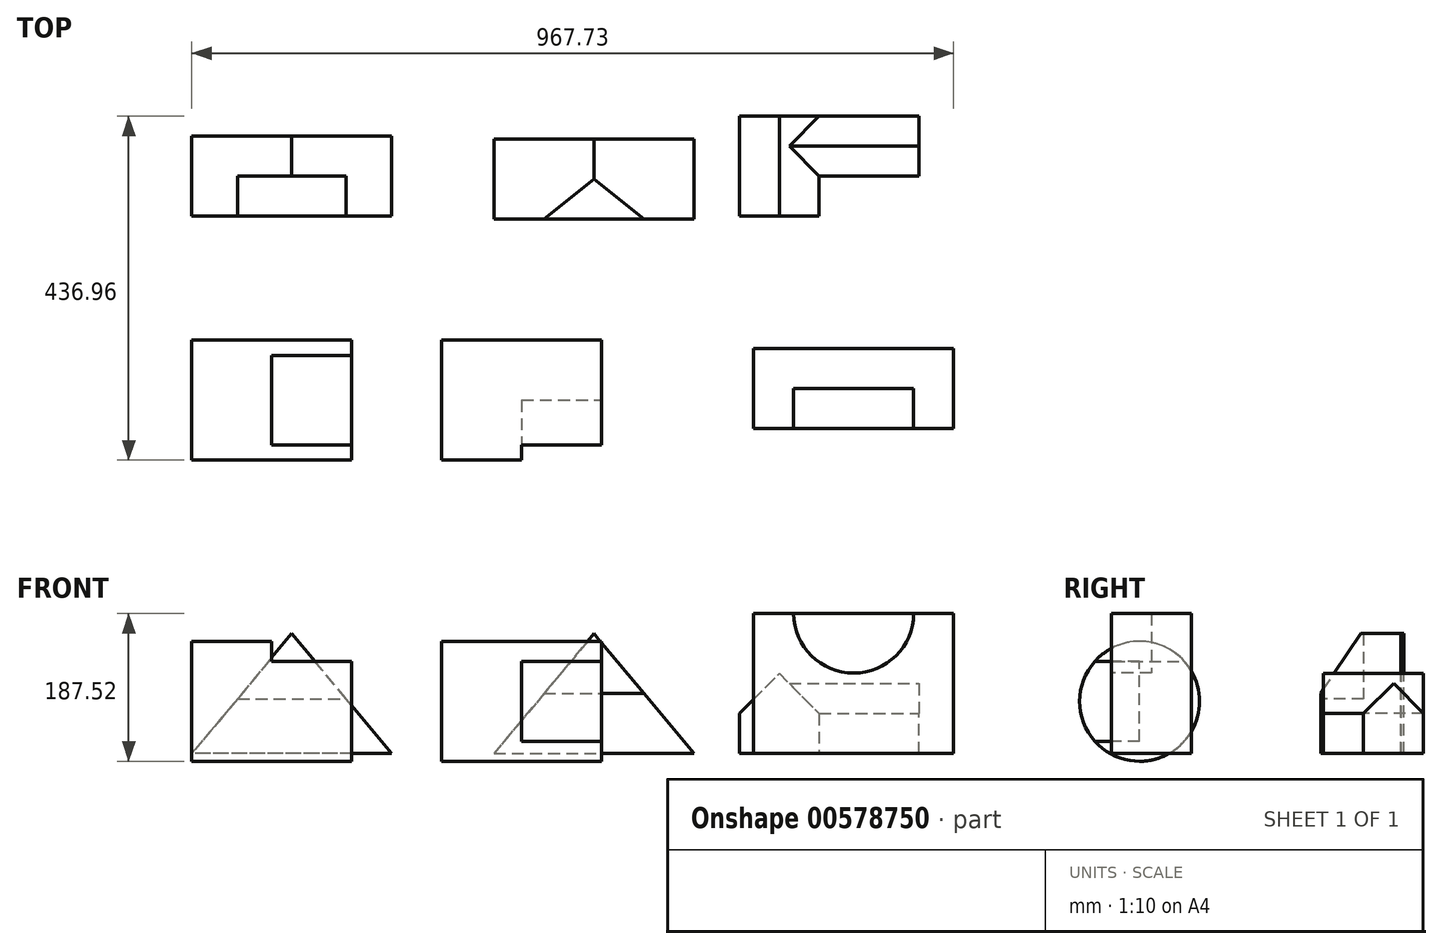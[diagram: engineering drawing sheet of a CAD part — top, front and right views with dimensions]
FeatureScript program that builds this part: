
annotation { "Feature Type Name" : "Feature", "Feature Type Description" : "" }
export const myFeature = defineFeature(function(context is Context, id is Id, definition is map)
    precondition{}
    {
        {
            var Q0;
            Q0=qCreatedBy(makeId("Right.planeOp"),FACE);
            var sketch = newSketch(context, id + "F0", { "sketchPlane" : qUnion([Q0])});
            skLineSegment(sketch, "E0", {"start": v(0, 0) * mm, "end": v(101.6, 0) * mm});
            skLineSegment(sketch, "E1", {"start": v(101.6, 0) * mm, "end": v(101.6, 152.4) * mm});
            skLineSegment(sketch, "E2", {"start": v(101.6, 152.4) * mm, "end": v(0, 152.4) * mm});
            skLineSegment(sketch, "E3", {"start": v(0, 152.4) * mm, "end": v(0, 0) * mm});
            skSolve(sketch);
        }
        {
            var Q0;
            Q0=makeQuery(id+"F0.imprint","IMPRINT",FACE,{"disambiguationData":[TD([[makeQuery(id+"F0.imprint","IMPRINT",EDGE,{"derivedFrom":sQuery(id+"F0.wireOp",EDGE,"E0")}),1.0]])]});
            extrude(context, id + "F1", {"entities" : qUnion([Q0]), "depth" : 254 * mm, "offsetDistance" : 25.4 * mm});
        }
        {
            var Q0;
            Q0=makeQuery(id+"F1.opExtrude","SWEPT_FACE",FACE,{"disambiguationData":[OSD([sQuery(id+"F0.wireOp",EDGE,"E3")])]});
            var sketch = newSketch(context, id + "F2", { "sketchPlane" : qUnion([Q0])});
            skLineSegment(sketch, "E4", {"start": v(127, 152.4) * mm, "end": v(0, 0) * mm});
            skLineSegment(sketch, "E5", {"start": v(0, 0) * mm, "end": v(254, 0) * mm});
            skLineSegment(sketch, "E6", {"start": v(254, 0) * mm, "end": v(127, 152.4) * mm});
            skSolve(sketch);
        }
        {
            var Q0;
            {var subQ0=sQuery(id+"F2.wireOp",EDGE,"E4");Q0=makeQuery(id+"F2.imprint","IMPRINT",FACE,{"disambiguationData":[TD([[makeQuery(id+"F2.imprint","IMPRINT",EDGE,{"derivedFrom":subQ0}),-1.0]])]});}
            extrude(context, id + "F3", {"entities" : qUnion([Q0]), "operationType" : NewBodyOperationType.REMOVE, "oppositeDirection" : true, "depth" : 101.6 * mm, "offsetDistance" : 25.4 * mm});
        }
        {
            var Q0;
            Q0=makeQuery(id+"F1.opExtrude","CAP_FACE",FACE,{"disambiguationData":[OSD([sQuery(id+"F0.wireOp",EDGE,"E0"),sQuery(id+"F0.wireOp",EDGE,"E1"),sQuery(id+"F0.wireOp",EDGE,"E2"),sQuery(id+"F0.wireOp",EDGE,"E3")])],"isStart":false});
            var sketch = newSketch(context, id + "F4", { "sketchPlane" : qUnion([Q0])});
            skLineSegment(sketch, "E7", {"start": v(0, 0) * mm, "end": v(0, 69.72) * mm});
            skLineSegment(sketch, "E8", {"start": v(0, 69.72) * mm, "end": v(50.8, 69.72) * mm});
            skLineSegment(sketch, "E9", {"start": v(50.8, 69.72) * mm, "end": v(50.8, 152.4) * mm});
            skLineSegment(sketch, "E10", {"start": v(50.8, 152.4) * mm, "end": v(101.6, 152.4) * mm});
            skLineSegment(sketch, "E11", {"start": v(101.6, 152.4) * mm, "end": v(101.6, 0) * mm});
            skLineSegment(sketch, "E12", {"start": v(101.6, 0) * mm, "end": v(0, 0) * mm});
            skSolve(sketch);
        }
        {
            var Q0;
            {var subQ0=sQuery(id+"F4.wireOp",EDGE,"E8");Q0=makeQuery(id+"F4.imprint","IMPRINT",FACE,{"disambiguationData":[TD([[makeQuery(id+"F4.imprint","IMPRINT",EDGE,{"derivedFrom":subQ0}),1.0]])]});}
            extrude(context, id + "F5", {"entities" : qUnion([Q0]), "operationType" : NewBodyOperationType.REMOVE, "oppositeDirection" : true, "depth" : 249.43 * mm, "offsetDistance" : 25.4 * mm});
        }
        {
            var Q0;
            Q0=qCreatedBy(makeId("Top.planeOp"),FACE);
            var sketch = newSketch(context, id + "F6", { "sketchPlane" : qUnion([Q0])});
            skLineSegment(sketch, "E13.bottom", {"start": v(383.68, -3.7) * mm, "end": v(637.68, -3.7) * mm});
            skLineSegment(sketch, "E13.top", {"start": v(383.68, 97.9) * mm, "end": v(637.68, 97.9) * mm});
            skLineSegment(sketch, "E13.left", {"start": v(383.68, -3.7) * mm, "end": v(383.68, 97.9) * mm});
            skLineSegment(sketch, "E13.right", {"start": v(637.68, -3.7) * mm, "end": v(637.68, 97.9) * mm});
            skSolve(sketch);
        }
        {
            var Q0;
            Q0=makeQuery(id+"F6.imprint","IMPRINT",FACE,{"disambiguationData":[TD([[makeQuery(id+"F6.imprint","IMPRINT",EDGE,{"derivedFrom":sQuery(id+"F6.wireOp",EDGE,"E13.bottom")}),1.0]])]});
            extrude(context, id + "F7", {"entities" : qUnion([Q0]), "depth" : 152.4 * mm, "offsetDistance" : 25.4 * mm});
        }
        {
            var Q0;
            Q0=makeQuery(id+"F7.opExtrude","SWEPT_FACE",FACE,{"disambiguationData":[OSD([sQuery(id+"F6.wireOp",EDGE,"E13.bottom")])]});
            var sketch = newSketch(context, id + "F8", { "sketchPlane" : qUnion([Q0])});
            skLineSegment(sketch, "E14", {"start": v(510.68, 0) * mm, "end": v(510.68, 152.4) * mm});
            skLineSegment(sketch, "E15", {"start": v(510.68, 152.4) * mm, "end": v(383.68, 0) * mm});
            skLineSegment(sketch, "E16", {"start": v(383.68, 0) * mm, "end": v(637.68, 0) * mm});
            skLineSegment(sketch, "E17", {"start": v(637.68, 0) * mm, "end": v(510.68, 152.4) * mm});
            skSolve(sketch);
        }
        {
            var Q0;
            {var subQ0=sQuery(id+"F8.wireOp",EDGE,"E15");Q0=makeQuery(id+"F8.imprint","IMPRINT",FACE,{"disambiguationData":[TD([[makeQuery(id+"F8.imprint","IMPRINT",EDGE,{"derivedFrom":subQ0}),-1.0]])]});}
            extrude(context, id + "F9", {"entities" : qUnion([Q0]), "operationType" : NewBodyOperationType.REMOVE, "oppositeDirection" : true, "depth" : 101.6 * mm, "offsetDistance" : 25.4 * mm});
        }
        {
            var Q0;
            Q0=makeQuery(id+"F7.opExtrude","SWEPT_FACE",FACE,{"disambiguationData":[OSD([sQuery(id+"F6.wireOp",EDGE,"E13.right")])]});
            var sketch = newSketch(context, id + "F10", { "sketchPlane" : qUnion([Q0])});
            skLineSegment(sketch, "E18", {"start": v(-3.7, 0) * mm, "end": v(-3.7, 76.2) * mm});
            skLineSegment(sketch, "E19", {"start": v(-3.7, 76.2) * mm, "end": v(47.1, 152.4) * mm});
            skSolve(sketch);
        }
        {
            var Q0;
            {var subQ0=sQuery(id+"F10.wireOp",EDGE,"E19");Q0=makeQuery(id+"F10.imprint","IMPRINT",FACE,{"disambiguationData":[TD([[makeQuery(id+"F10.imprint","IMPRINT",EDGE,{"derivedFrom":subQ0}),1.0]])]});}
            extrude(context, id + "F11", {"entities" : qUnion([Q0]), "operationType" : NewBodyOperationType.REMOVE, "oppositeDirection" : true, "depth" : 205.5 * mm, "offsetDistance" : 25.4 * mm});
        }
        {
            var Q0;
            Q0=makeQuery(id+"F7.opExtrude","SWEPT_FACE",FACE,{"disambiguationData":[OSD([sQuery(id+"F6.wireOp",EDGE,"E13.top")])]});
            var sketch = newSketch(context, id + "F12", { "sketchPlane" : qUnion([Q0])});
            skLineSegment(sketch, "E20", {"start": v(-637.68, 0) * mm, "end": v(-510.68, 152.4) * mm});
            skSolve(sketch);
        }
        {
            var Q0;
            Q0=makeQuery(id+"F12.imprint","IMPRINT",FACE,{"disambiguationData":[TD([[makeQuery(id+"F12.imprint","IMPRINT",EDGE,{"derivedFrom":sQuery(id+"F12.wireOp",EDGE,"E20")}),1.0]])]});
            extrude(context, id + "F13", {"entities" : qUnion([Q0]), "operationType" : NewBodyOperationType.REMOVE, "oppositeDirection" : true, "depth" : 152.4 * mm, "offsetDistance" : 25.4 * mm});
        }
        {
            var Q0;
            Q0=makeQuery(id+"F1.opExtrude","SWEPT_FACE",FACE,{"disambiguationData":[OSD([sQuery(id+"F0.wireOp",EDGE,"E1")])]});
            var sketch = newSketch(context, id + "F14", { "sketchPlane" : qUnion([Q0])});
            skLineSegment(sketch, "E21", {"start": v(-254, 0) * mm, "end": v(-127, 152.4) * mm});
            skSolve(sketch);
        }
        {
            var Q0;
            Q0=makeQuery(id+"F14.imprint","IMPRINT",FACE,{"disambiguationData":[TD([[makeQuery(id+"F14.imprint","IMPRINT",EDGE,{"derivedFrom":sQuery(id+"F14.wireOp",EDGE,"E21")}),1.0]])]});
            extrude(context, id + "F15", {"entities" : qUnion([Q0]), "operationType" : NewBodyOperationType.REMOVE, "oppositeDirection" : true, "depth" : 444.5 * mm, "offsetDistance" : 25.4 * mm});
        }
        {
            var Q0;
            Q0=qCreatedBy(makeId("Front.planeOp"),FACE);
            var sketch = newSketch(context, id + "F16", { "sketchPlane" : qUnion([Q0])});
            skLineSegment(sketch, "E22", {"start": v(695.37, 0) * mm, "end": v(695.37, 50.8) * mm});
            skLineSegment(sketch, "E23", {"start": v(695.37, 50.8) * mm, "end": v(746.17, 101.6) * mm});
            skLineSegment(sketch, "E24", {"start": v(746.17, 101.6) * mm, "end": v(796.97, 50.8) * mm});
            skLineSegment(sketch, "E25", {"start": v(796.97, 50.8) * mm, "end": v(796.97, 0) * mm});
            skLineSegment(sketch, "E26", {"start": v(695.37, 0) * mm, "end": v(796.97, 0) * mm});
            skSolve(sketch);
        }
        {
            var Q0;
            Q0 = qSketchRegion(id + "F16", true);
            extrude(context, id + "F17", {"entities" : qUnion([Q0]), "oppositeDirection" : true, "depth" : 127 * mm, "offsetDistance" : 25.4 * mm});
        }
        {
            var Q0;
            Q0=makeQuery(id+"F17.opExtrude","SWEPT_FACE",FACE,{"disambiguationData":[OSD([sQuery(id+"F16.wireOp",EDGE,"E25")])]});
            cPlane(context, id + "F18", {"entities" : qUnion([Q0]), "cplaneType" : CPlaneType.OFFSET, "offset" : 127 * mm, "width" : 152.4 * mm, "height" : 152.4 * mm});
        }
        {
            var Q0;
            Q0=qCreatedBy(id+"F18.planeOp",FACE);
            var sketch = newSketch(context, id + "F19", { "sketchPlane" : qUnion([Q0])});
            skLineSegment(sketch, "E27", {"start": v(0, 0) * mm, "end": v(127, 0) * mm});
            skLineSegment(sketch, "E28", {"start": v(0, 0) * mm, "end": v(0, 50.8) * mm});
            skLineSegment(sketch, "E29", {"start": v(50.8, 50.8) * mm, "end": v(50.8, 0) * mm});
            skLineSegment(sketch, "E30", {"start": v(50.8, 0) * mm, "end": v(0, 0) * mm});
            skLineSegment(sketch, "E31", {"start": v(127, 0) * mm, "end": v(127, 50.8) * mm});
            skLineSegment(sketch, "E32", {"start": v(50.8, 0) * mm, "end": v(127, 0) * mm});
            skLineSegment(sketch, "E33", {"start": v(88.9, 88.9) * mm, "end": v(50.8, 50.8) * mm});
            skLineSegment(sketch, "E34", {"start": v(88.9, 88.9) * mm, "end": v(127, 50.8) * mm});
            skSolve(sketch);
        }
        {
            var Q0;
            Q0=makeQuery(id+"F19.imprint","IMPRINT",FACE,{"disambiguationData":[TD([[makeQuery(id+"F19.imprint","IMPRINT",EDGE,{"derivedFrom":sQuery(id+"F19.wireOp",EDGE,"E29")}),1.0]])]});
            extrude(context, id + "F20", {"entities" : qUnion([Q0]), "operationType" : NewBodyOperationType.ADD, "endBound" : BoundingType.UP_TO_NEXT, "oppositeDirection" : true, "depth" : 25.4 * mm, "offsetDistance" : 25.4 * mm});
        }
        {
            var Q0;
            Q0=qCreatedBy(makeId("Right.planeOp"),FACE);
            var sketch = newSketch(context, id + "F21", { "sketchPlane" : qUnion([Q0])});
            skCircle(sketch, "E35", {"center": v(-233.71, 66.48) * mm, "radius": 76.2 * mm});
            skSolve(sketch);
        }
        {
            var Q0;
            Q0=makeQuery(id+"F21.imprint","IMPRINT",FACE,{"disambiguationData":[TD([[makeQuery(id+"F21.imprint","IMPRINT",EDGE,{"derivedFrom":sQuery(id+"F21.wireOp",EDGE,"E35")}),1.0]])]});
            extrude(context, id + "F22", {"entities" : qUnion([Q0]), "depth" : 203.2 * mm, "offsetDistance" : 25.4 * mm});
        }
        {
            var Q0;
            Q0=makeQuery(id+"F22.opExtrude","CAP_FACE",FACE,{"disambiguationData":[OSD([sQuery(id+"F21.wireOp",EDGE,"E35")])],"isStart":false});
            var sketch = newSketch(context, id + "F23", { "sketchPlane" : qUnion([Q0])});
            skPoint(sketch, "E36.orphan", {"position": v(-233.71, 66.48) * mm});
            skArc(sketch, "E37", {"start": v(-176.92, 117.28) * mm, "mid": v(-233.71, 142.68) * mm, "end": v(-290.5, 117.28) * mm});
            skLineSegment(sketch, "E38", {"start": v(-290.5, 117.28) * mm, "end": v(-176.92, 117.28) * mm});
            skSolve(sketch);
        }
        {
            var Q0;
            Q0=makeQuery(id+"F23.imprint","IMPRINT",FACE,{"disambiguationData":[TD([[makeQuery(id+"F23.imprint","IMPRINT",EDGE,{"derivedFrom":sQuery(id+"F23.wireOp",EDGE,"E37")}),1.0]])]});
            extrude(context, id + "F24", {"entities" : qUnion([Q0]), "operationType" : NewBodyOperationType.REMOVE, "oppositeDirection" : true, "depth" : 101.6 * mm, "offsetDistance" : 25.4 * mm});
        }
        {
            var Q0;
            Q0=makeQuery(id+"F22.opExtrude","CAP_FACE",FACE,{"disambiguationData":[OSD([sQuery(id+"F21.wireOp",EDGE,"E35")])],"isStart":false});
            cPlane(context, id + "F25", {"entities" : qUnion([Q0]), "cplaneType" : CPlaneType.OFFSET, "offset" : 114.3 * mm, "width" : 152.4 * mm, "height" : 152.4 * mm});
        }
        {
            var Q0;
            Q0=qCreatedBy(id+"F25.planeOp",FACE);
            var sketch = newSketch(context, id + "F26", { "sketchPlane" : qUnion([Q0])});
            skCircle(sketch, "E39", {"center": v(-233.76, 66.48) * mm, "radius": 76.2 * mm});
            skSolve(sketch);
        }
        {
            var Q0;
            Q0=makeQuery(id+"F26.imprint","IMPRINT",FACE,{"disambiguationData":[TD([[makeQuery(id+"F26.imprint","IMPRINT",EDGE,{"derivedFrom":sQuery(id+"F26.wireOp",EDGE,"E39")}),1.0]])]});
            extrude(context, id + "F27", {"entities" : qUnion([Q0]), "depth" : 203.2 * mm, "offsetDistance" : 25.4 * mm});
        }
        {
            var Q0;
            Q0=makeQuery(id+"F27.opExtrude","CAP_FACE",FACE,{"disambiguationData":[OSD([sQuery(id+"F26.wireOp",EDGE,"E39")])],"isStart":false});
            var sketch = newSketch(context, id + "F28", { "sketchPlane" : qUnion([Q0])});
            skLineSegment(sketch, "E40", {"start": v(-233.76, 66.48) * mm, "end": v(-233.76, 15.68) * mm});
            skLineSegment(sketch, "E41", {"start": v(-233.76, 66.48) * mm, "end": v(-233.76, 117.28) * mm});
            skLineSegment(sketch, "E42", {"start": v(-233.76, 117.28) * mm, "end": v(-290.56, 117.28) * mm});
            skLineSegment(sketch, "E43", {"start": v(-233.76, 15.68) * mm, "end": v(-290.56, 15.68) * mm});
            skSolve(sketch);
        }
        {
            var Q0;
            Q0=makeQuery(id+"F28.imprint","IMPRINT",FACE,{"disambiguationData":[TD([[makeQuery(id+"F28.imprint","IMPRINT",EDGE,{"derivedFrom":sQuery(id+"F28.wireOp",EDGE,"E41")}),1.0]])]});
            extrude(context, id + "F29", {"entities" : qUnion([Q0]), "operationType" : NewBodyOperationType.REMOVE, "oppositeDirection" : true, "depth" : 101.6 * mm, "offsetDistance" : 25.4 * mm});
        }
        {
            var Q0;
            Q0=qCreatedBy(makeId("Top.planeOp"),FACE);
            var sketch = newSketch(context, id + "F30", { "sketchPlane" : qUnion([Q0])});
            skLineSegment(sketch, "E44.bottom", {"start": v(713.73, -167.83) * mm, "end": v(967.73, -167.83) * mm});
            skLineSegment(sketch, "E44.top", {"start": v(713.73, -269.43) * mm, "end": v(967.73, -269.43) * mm});
            skLineSegment(sketch, "E44.left", {"start": v(713.73, -167.83) * mm, "end": v(713.73, -269.43) * mm});
            skLineSegment(sketch, "E44.right", {"start": v(967.73, -167.83) * mm, "end": v(967.73, -269.43) * mm});
            skSolve(sketch);
        }
        {
            var Q0;
            Q0=makeQuery(id+"F30.imprint","IMPRINT",FACE,{"disambiguationData":[TD([[makeQuery(id+"F30.imprint","IMPRINT",EDGE,{"derivedFrom":sQuery(id+"F30.wireOp",EDGE,"E44.bottom")}),-1.0]])]});
            extrude(context, id + "F31", {"entities" : qUnion([Q0]), "depth" : 177.8 * mm, "offsetDistance" : 25.4 * mm});
        }
        {
            var Q0;
            Q0=makeQuery(id+"F31.opExtrude","SWEPT_FACE",FACE,{"disambiguationData":[OSD([sQuery(id+"F30.wireOp",EDGE,"E44.top")])]});
            var sketch = newSketch(context, id + "F32", { "sketchPlane" : qUnion([Q0])});
            skArc(sketch, "E45", {"start": v(764.53, 177.8) * mm, "mid": v(840.73, 102.34) * mm, "end": v(916.93, 177.8) * mm});
            skSolve(sketch);
        }
        {
            var Q0;
            {var subQ0=sQuery(id+"F32.wireOp",EDGE,"E45");Q0=makeQuery(id+"F32.imprint","IMPRINT",FACE,{"disambiguationData":[TD([[makeQuery(id+"F32.imprint","IMPRINT",EDGE,{"derivedFrom":subQ0}),1.0]])]});}
            extrude(context, id + "F33", {"entities" : qUnion([Q0]), "operationType" : NewBodyOperationType.REMOVE, "oppositeDirection" : true, "depth" : 50.8 * mm, "offsetDistance" : 25.4 * mm});
        }
    });
